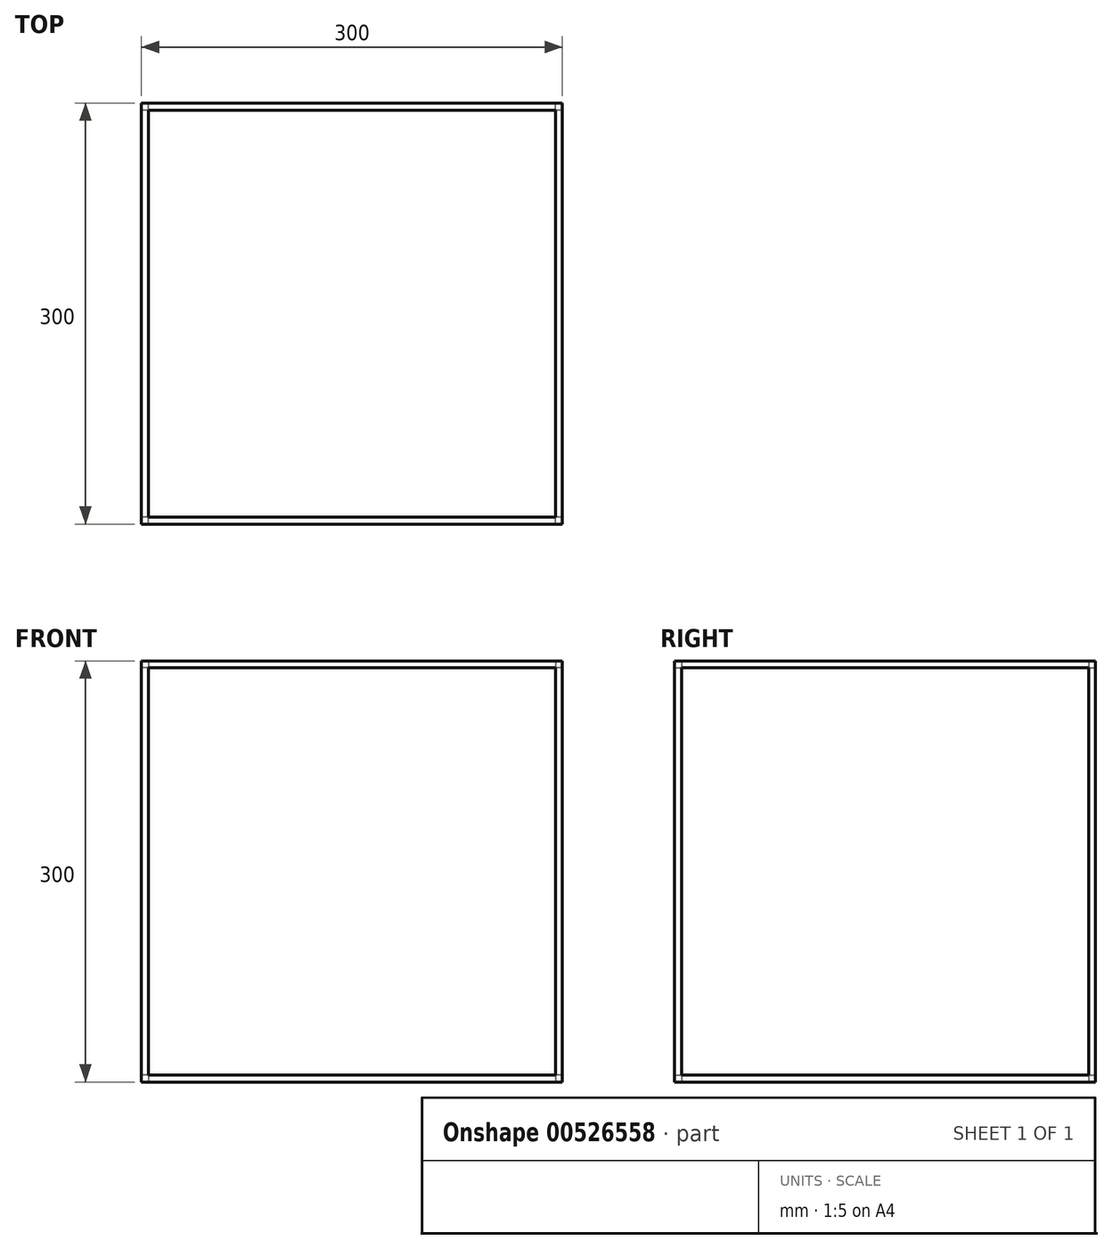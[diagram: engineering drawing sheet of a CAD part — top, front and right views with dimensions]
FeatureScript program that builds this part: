
annotation { "Feature Type Name" : "Feature", "Feature Type Description" : "" }
export const myFeature = defineFeature(function(context is Context, id is Id, definition is map)
    precondition{}
    {
        {
            var Q0;
            Q0=qCreatedBy(makeId("Top.planeOp"),FACE);
            var sketch = newSketch(context, id + "F0", { "sketchPlane" : qUnion([Q0])});
            skLineSegment(sketch, "E0.bottom", {"start": v(-150, 150) * mm, "end": v(150, 150) * mm});
            skLineSegment(sketch, "E0.top", {"start": v(-150, -150) * mm, "end": v(150, -150) * mm});
            skLineSegment(sketch, "E0.left", {"start": v(-150, 150) * mm, "end": v(-150, -150) * mm});
            skLineSegment(sketch, "E0.right", {"start": v(150, 150) * mm, "end": v(150, -150) * mm});
            skPoint(sketch, "E0.middle", {"position": v(0, 0) * mm});
            skLineSegment(sketch, "E1.bottom", {"start": v(-145, 145) * mm, "end": v(145, 145) * mm});
            skLineSegment(sketch, "E1.top", {"start": v(-145, -145) * mm, "end": v(145, -145) * mm});
            skLineSegment(sketch, "E1.left", {"start": v(-145, 145) * mm, "end": v(-145, -145) * mm});
            skLineSegment(sketch, "E1.right", {"start": v(145, 145) * mm, "end": v(145, -145) * mm});
            skSolve(sketch);
        }
        {
            var Q0;
            Q0=qSketchRegion(id+"F0",true);
            extrude(context, id + "F1", {"entities" : qUnion([Q0]), "depth" : 300 * mm});
        }
        {
            var Q0;
            Q0=qCreatedBy(makeId("Front.planeOp"),FACE);
            var sketch = newSketch(context, id + "F2", { "sketchPlane" : qUnion([Q0])});
            skLineSegment(sketch, "E2.bottom", {"start": v(145, 295) * mm, "end": v(-145, 295) * mm});
            skLineSegment(sketch, "E2.top", {"start": v(145, 5) * mm, "end": v(-145, 5) * mm});
            skLineSegment(sketch, "E2.left", {"start": v(145, 295) * mm, "end": v(145, 5) * mm});
            skLineSegment(sketch, "E2.right", {"start": v(-145, 295) * mm, "end": v(-145, 5) * mm});
            skSolve(sketch);
        }
        {
            var Q0;
            Q0=qSketchRegion(id+"F2",true);
            extrude(context, id + "F3", {"entities" : qUnion([Q0]), "operationType" : NewBodyOperationType.REMOVE, "endBound" : BoundingType.SYMMETRIC, "depth" : 300 * mm, "offsetDistance" : 25 * mm});
        }
        {
            var Q0;
            Q0=qCreatedBy(makeId("Right.planeOp"),FACE);
            var sketch = newSketch(context, id + "F4", { "sketchPlane" : qUnion([Q0])});
            skLineSegment(sketch, "E3.bottom", {"start": v(-145, 295) * mm, "end": v(145, 295) * mm});
            skLineSegment(sketch, "E3.top", {"start": v(-145, 5) * mm, "end": v(145, 5) * mm});
            skLineSegment(sketch, "E3.left", {"start": v(-145, 295) * mm, "end": v(-145, 5) * mm});
            skLineSegment(sketch, "E3.right", {"start": v(145, 295) * mm, "end": v(145, 5) * mm});
            skSolve(sketch);
        }
        {
            var Q0;
            Q0=qSketchRegion(id+"F4",true);
            extrude(context, id + "F5", {"entities" : qUnion([Q0]), "operationType" : NewBodyOperationType.REMOVE, "endBound" : BoundingType.SYMMETRIC, "depth" : 300 * mm, "offsetDistance" : 25 * mm});
        }
    });
